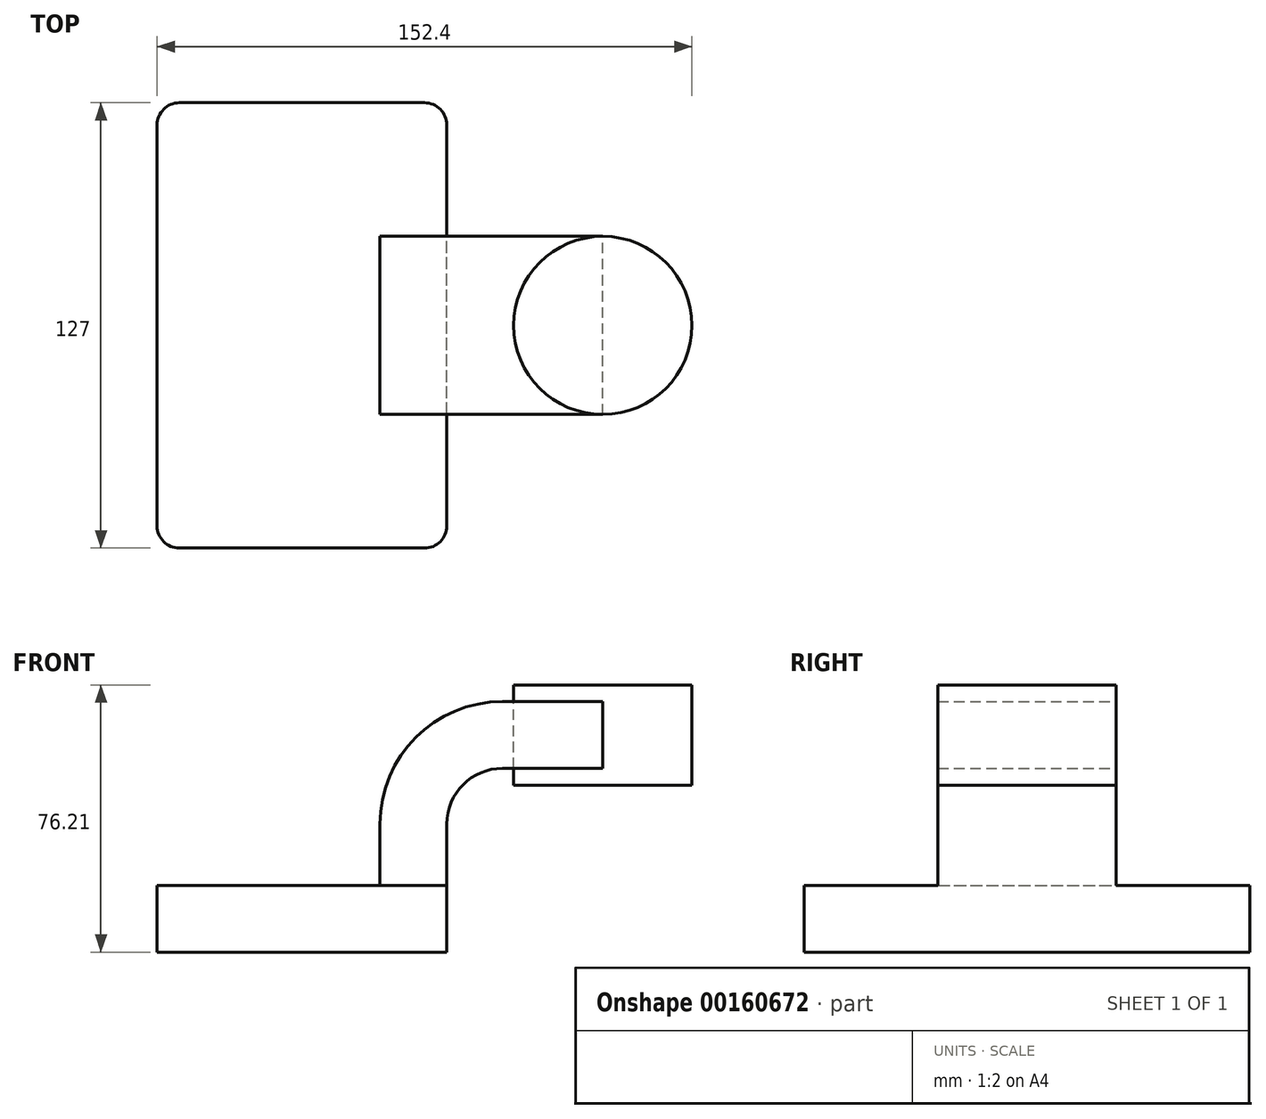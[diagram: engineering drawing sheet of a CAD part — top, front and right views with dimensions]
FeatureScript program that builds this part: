
annotation { "Feature Type Name" : "Feature", "Feature Type Description" : "" }
export const myFeature = defineFeature(function(context is Context, id is Id, definition is map)
    precondition{}
    {
        {
            var Q0;
            Q0=qCreatedBy(makeId("Front.planeOp"),FACE);
            var sketch = newSketch(context, id + "F0", { "sketchPlane" : qUnion([Q0])});
            skLineSegment(sketch, "E0.bottom", {"start": v(41.28, 9.53) * mm, "end": v(-41.28, 9.52) * mm});
            skLineSegment(sketch, "E0.top", {"start": v(41.28, -9.52) * mm, "end": v(-41.27, -9.53) * mm});
            skLineSegment(sketch, "E0.left", {"start": v(41.27, 9.53) * mm, "end": v(41.28, -9.52) * mm});
            skLineSegment(sketch, "E0.right", {"start": v(-41.28, 9.52) * mm, "end": v(-41.28, -9.53) * mm});
            skPoint(sketch, "E0.middle", {"position": v(0, 0) * mm});
            skLineSegment(sketch, "E1", {"start": v(41.28, 9.53) * mm, "end": v(41.28, 27) * mm});
            skArc(sketch, "E2", {"start": v(41.27, 27) * mm, "mid": v(45.92, 38.23) * mm, "end": v(57.15, 42.88) * mm});
            skLineSegment(sketch, "E3", {"start": v(57.15, 42.88) * mm, "end": v(85.72, 42.88) * mm});
            skLineSegment(sketch, "E4.bottom", {"start": v(60.33, 38.1) * mm, "end": v(111.12, 38.1) * mm});
            skLineSegment(sketch, "E4.top", {"start": v(60.33, 66.68) * mm, "end": v(111.12, 66.68) * mm});
            skLineSegment(sketch, "E4.left", {"start": v(60.33, 38.1) * mm, "end": v(60.33, 66.68) * mm});
            skLineSegment(sketch, "E4.right", {"start": v(111.12, 38.1) * mm, "end": v(111.12, 66.68) * mm});
            skPoint(sketch, "E4.middle", {"position": v(85.72, 52.39) * mm});
            skArc(sketch, "E5.0", {"start": v(41.46, 27) * mm, "mid": v(46.06, 38.1) * mm, "end": v(57.15, 42.69) * mm});
            skLineSegment(sketch, "E5.1", {"start": v(41.46, 9.53) * mm, "end": v(41.46, 27) * mm});
            skLineSegment(sketch, "E6.0", {"start": v(57.15, 61.93) * mm, "end": v(85.72, 61.93) * mm});
            skArc(sketch, "E6.1", {"start": v(22.23, 27) * mm, "mid": v(32.45, 51.7) * mm, "end": v(57.15, 61.93) * mm});
            skLineSegment(sketch, "E6.2", {"start": v(22.23, 9.53) * mm, "end": v(22.23, 27) * mm});
            skLineSegment(sketch, "E7", {"start": v(85.72, 66.68) * mm, "end": v(85.72, 38.1) * mm});
            skFitSpline(sketch, "E8", {"points": [v(-41.28, 9.52) * mm, v(57.15, 61.93) * mm], "startDerivative": vector(3.8, 85.28) * mm, "endDerivative": vector(97.95, -0.52) * mm});
            skSolve(sketch);
        }
        {
            var Q0;
            Q0=makeQuery(id+"F0.imprint","IMPRINT",FACE,{"disambiguationData":[TD([[makeQuery(id+"F0.imprint","IMPRINT",EDGE,{"derivedFrom":sQuery(id+"F0.wireOp",EDGE,"E0.top")}),-1.0]])]});
            extrude(context, id + "F1", {"entities" : qUnion([Q0]), "endBound" : BoundingType.SYMMETRIC, "depth" : 127 * mm});
        }
        {
            var Q0;
            {var subQ7=sQuery(id+"F0.wireOp",EDGE,"E1");Q0=makeQuery(id+"F0.imprint","IMPRINT",FACE,{"disambiguationData":[TD([[makeQuery(id+"F0.imprint","IMPRINT",EDGE,{"derivedFrom":subQ7}),1.0]])]});}
            var Q1;
            {var subQ0=sQuery(id+"F0.wireOp",EDGE,"E7");var subQ1=sQuery(id+"F0.wireOp",EDGE,"E3");var subQ2=makeQuery(id+"F0.imprint","INTERSECT",VERTEX,{"derivedFrom":[subQ1,subQ0]});Q1=makeQuery(id+"F0.imprint","IMPRINT",FACE,{"disambiguationData":[TD([[makeQuery(id+"F0.imprint","IMPRINT",EDGE,{"disambiguationData":[TD([[subQ2,1.0]])],"derivedFrom":subQ1}),1.0]])]});}
            extrude(context, id + "F2", {"entities" : qUnion([Q0, Q1]), "operationType" : NewBodyOperationType.ADD, "endBound" : BoundingType.SYMMETRIC, "depth" : 50.8 * mm});
        }
        {
            var Q0;
            Q0=makeQuery(id+"F0.imprint","IMPRINT",FACE,{"disambiguationData":[TD([[makeQuery(id+"F0.imprint","IMPRINT",EDGE,{"derivedFrom":sQuery(id+"F0.wireOp",EDGE,"E6.1")}),1.0]])]});
            extrude(context, id + "F3", {"entities" : qUnion([Q0]), "operationType" : NewBodyOperationType.ADD, "endBound" : BoundingType.SYMMETRIC, "depth" : 15.88 * mm});
        }
        {
            var Q0;
            {var subQ4=sQuery(id+"F0.wireOp",EDGE,"E4.right");Q0=makeQuery(id+"F0.imprint","IMPRINT",FACE,{"disambiguationData":[TD([[makeQuery(id+"F0.imprint","IMPRINT",EDGE,{"derivedFrom":subQ4}),1.0]])]});}
            var Q1;
            Q1=sQuery(id+"F0.wireOp",EDGE,"E7");
            revolve(context, id + "F4", {"entities" : qUnion([Q0]), "axis" : qUnion([Q1]), "revolveType" : RevolveType.FULL});
        }
        {
            var Q0;
            Q0=makeQuery(id+"F1.opExtrude","CAP_EDGE",EDGE,{"disambiguationData":[OSD([sQuery(id+"F0.wireOp",EDGE,"E0.left")])],"isStart":false});
            var Q1;
            Q1=makeQuery(id+"F1.opExtrude","CAP_EDGE",EDGE,{"disambiguationData":[OSD([sQuery(id+"F0.wireOp",EDGE,"E0.right")])],"isStart":false});
            var Q2;
            Q2=makeQuery(id+"F1.opExtrude","CAP_EDGE",EDGE,{"disambiguationData":[OSD([sQuery(id+"F0.wireOp",EDGE,"E0.left")])],"isStart":true});
            var Q3;
            Q3=makeQuery(id+"F1.opExtrude","CAP_EDGE",EDGE,{"disambiguationData":[OSD([sQuery(id+"F0.wireOp",EDGE,"E0.right")])],"isStart":true});
            fillet(context, id + "F5", {"entities" : qUnion([Q0, Q1, Q2, Q3]), "radius" : 6.35 * mm, "tangentPropagation" : true, "allowEdgeOverflow" : false});
        }
    });
